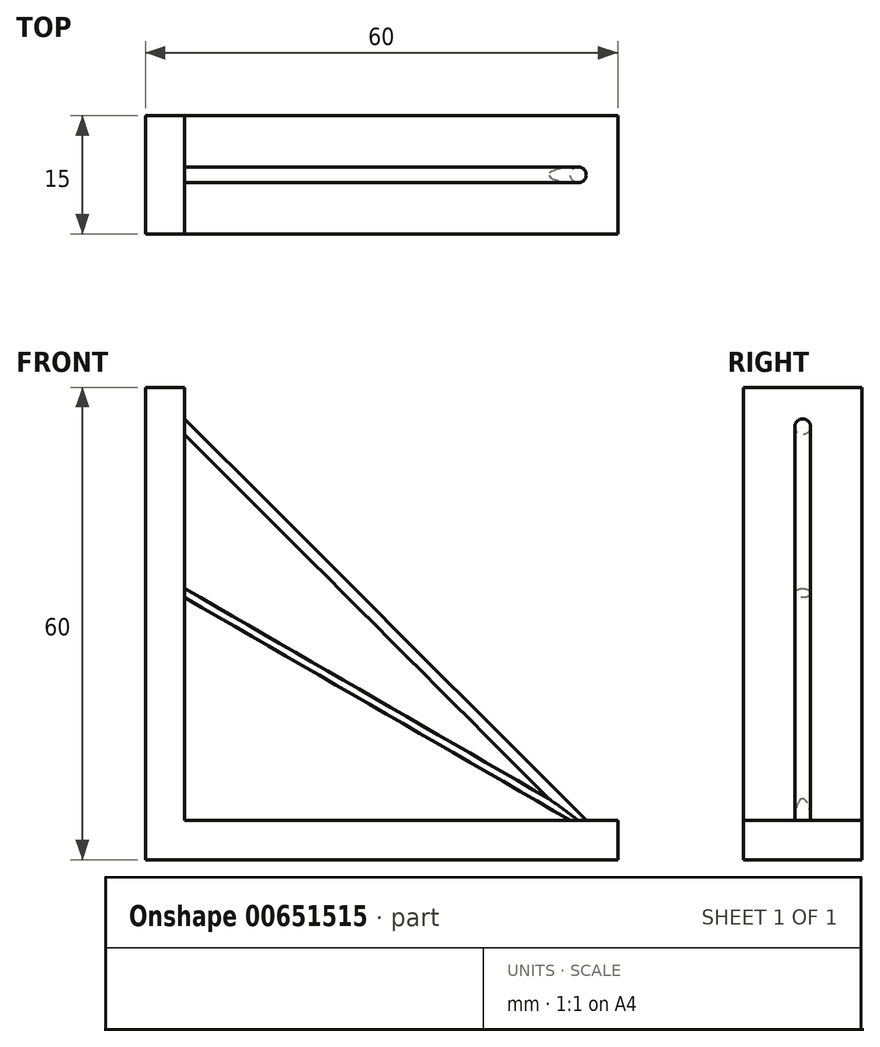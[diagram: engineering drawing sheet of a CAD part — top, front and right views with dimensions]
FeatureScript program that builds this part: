
annotation { "Feature Type Name" : "Feature", "Feature Type Description" : "" }
export const myFeature = defineFeature(function(context is Context, id is Id, definition is map)
    precondition{}
    {
        {
            var Q0;
            Q0=qCreatedBy(makeId("Front.planeOp"),FACE);
            var sketch = newSketch(context, id + "F0", { "sketchPlane" : qUnion([Q0])});
            skLineSegment(sketch, "E0.bottom", {"start": v(0, 0) * mm, "end": v(60, 0) * mm});
            skLineSegment(sketch, "E0.top", {"start": v(5, 5) * mm, "end": v(60, 5) * mm});
            skLineSegment(sketch, "E0.left", {"start": v(0, 0) * mm, "end": v(0, 5) * mm});
            skLineSegment(sketch, "E0.right", {"start": v(60, 0) * mm, "end": v(60, 5) * mm});
            skLineSegment(sketch, "E1.bottom", {"start": v(0, 0) * mm, "end": v(5, 0) * mm});
            skLineSegment(sketch, "E1.top", {"start": v(0, 60) * mm, "end": v(5, 60) * mm});
            skLineSegment(sketch, "E1.left", {"start": v(0, 0) * mm, "end": v(0, 60) * mm});
            skLineSegment(sketch, "E1.right", {"start": v(5, 5) * mm, "end": v(5, 60) * mm});
            skSolve(sketch);
        }
        {
            var Q0;
            Q0=makeQuery(id+"F0.imprint","IMPRINT",FACE,{"disambiguationData":[TD([[makeQuery(id+"F0.imprint","IMPRINT",EDGE,{"derivedFrom":sQuery(id+"F0.wireOp",EDGE,"E0.bottom")}),1.0]])]});
            extrude(context, id + "F1", {"entities" : qUnion([Q0]), "depth" : 15 * mm, "offsetDistance" : 25 * mm});
        }
        {
            var Q0;
            Q0=makeQuery(id+"F1.opExtrude","SWEPT_FACE",FACE,{"disambiguationData":[OSD([sQuery(id+"F0.wireOp",EDGE,"E0.top")])]});
            var sketch = newSketch(context, id + "F2", { "sketchPlane" : qUnion([Q0])});
            skCircle(sketch, "E2", {"center": v(55, -7.5) * mm, "radius": 1 * mm});
            skSolve(sketch);
        }
        {
            var Q0;
            Q0=qCreatedBy(makeId("Front.planeOp"),FACE);
            var sketch = newSketch(context, id + "F3", { "sketchPlane" : qUnion([Q0])});
            skLineSegment(sketch, "E3", {"start": v(55, 3) * mm, "end": v(1.97, 56.03) * mm});
            skSolve(sketch);
        }
        {
            var Q0;
            Q0 = qSketchRegion(id + "F2", true);
            var Q1;
            Q1 = qConstructionFilter(qBodyType(qCreatedBy(id + "F3" ,EDGE), BodyType.WIRE), ConstructionObject.NO);
            sweep(context, id + "F4", {"operationType" : NewBodyOperationType.ADD, "profiles" : qUnion([Q0]), "path" : qUnion([Q1])});
        }
        {
            var Q0;
            Q0=qCreatedBy(makeId("Front.planeOp"),FACE);
            var sketch = newSketch(context, id + "F5", { "sketchPlane" : qUnion([Q0])});
            skLineSegment(sketch, "E4", {"start": v(54.6, 5) * mm, "end": v(2.64, 35) * mm});
            skSolve(sketch);
        }
        {
            var Q0;
            Q0 = qSketchRegion(id + "F2", true);
            var Q1;
            Q1 = qConstructionFilter(qBodyType(qCreatedBy(id + "F5" ,EDGE), BodyType.WIRE), ConstructionObject.NO);
            sweep(context, id + "F6", {"operationType" : NewBodyOperationType.ADD, "profiles" : qUnion([Q0]), "path" : qUnion([Q1])});
        }
    });
